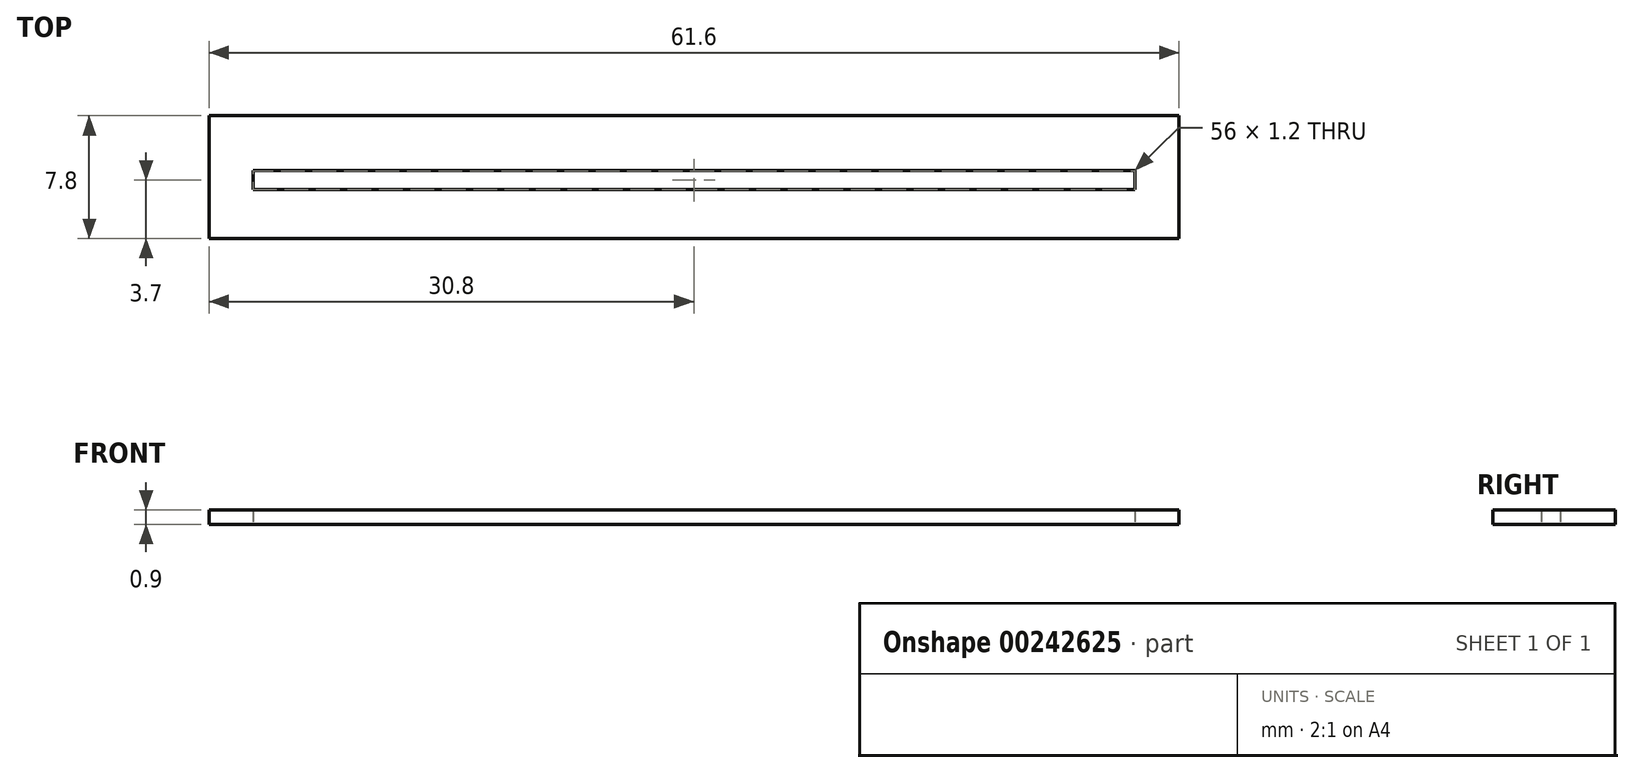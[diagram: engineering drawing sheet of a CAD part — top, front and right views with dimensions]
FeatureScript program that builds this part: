
annotation { "Feature Type Name" : "Feature", "Feature Type Description" : "" }
export const myFeature = defineFeature(function(context is Context, id is Id, definition is map)
    precondition{}
    {
        {
            var Q0;
            Q0=qCreatedBy(makeId("Top.planeOp"),FACE);
            var sketch = newSketch(context, id + "F0", { "sketchPlane" : qUnion([Q0])});
            skLineSegment(sketch, "E0.bottom", {"start": v(30.8, -3.9) * mm, "end": v(-30.8, -3.9) * mm});
            skLineSegment(sketch, "E0.top", {"start": v(30.8, 3.9) * mm, "end": v(-30.8, 3.9) * mm});
            skLineSegment(sketch, "E0.left", {"start": v(30.8, -3.9) * mm, "end": v(30.8, 3.9) * mm});
            skLineSegment(sketch, "E0.right", {"start": v(-30.8, -3.9) * mm, "end": v(-30.8, 3.9) * mm});
            skPoint(sketch, "E0.middle", {"position": v(0, 0) * mm});
            skLineSegment(sketch, "E1.bottom", {"start": v(28, -0.8) * mm, "end": v(-28, -0.8) * mm});
            skLineSegment(sketch, "E1.top", {"start": v(28, 0.4) * mm, "end": v(-28, 0.4) * mm});
            skLineSegment(sketch, "E1.left", {"start": v(28, -0.8) * mm, "end": v(28, 0.4) * mm});
            skLineSegment(sketch, "E1.right", {"start": v(-28, -0.8) * mm, "end": v(-28, 0.4) * mm});
            skPoint(sketch, "E1.middle", {"position": v(0, -0.2) * mm});
            skSolve(sketch);
        }
        {
            var Q0;
            Q0 = qSketchRegion(id + "F0", true);
            extrude(context, id + "F1", {"entities" : qUnion([Q0]), "depth" : 0.9 * mm, "offsetDistance" : 25 * mm});
        }
    });
